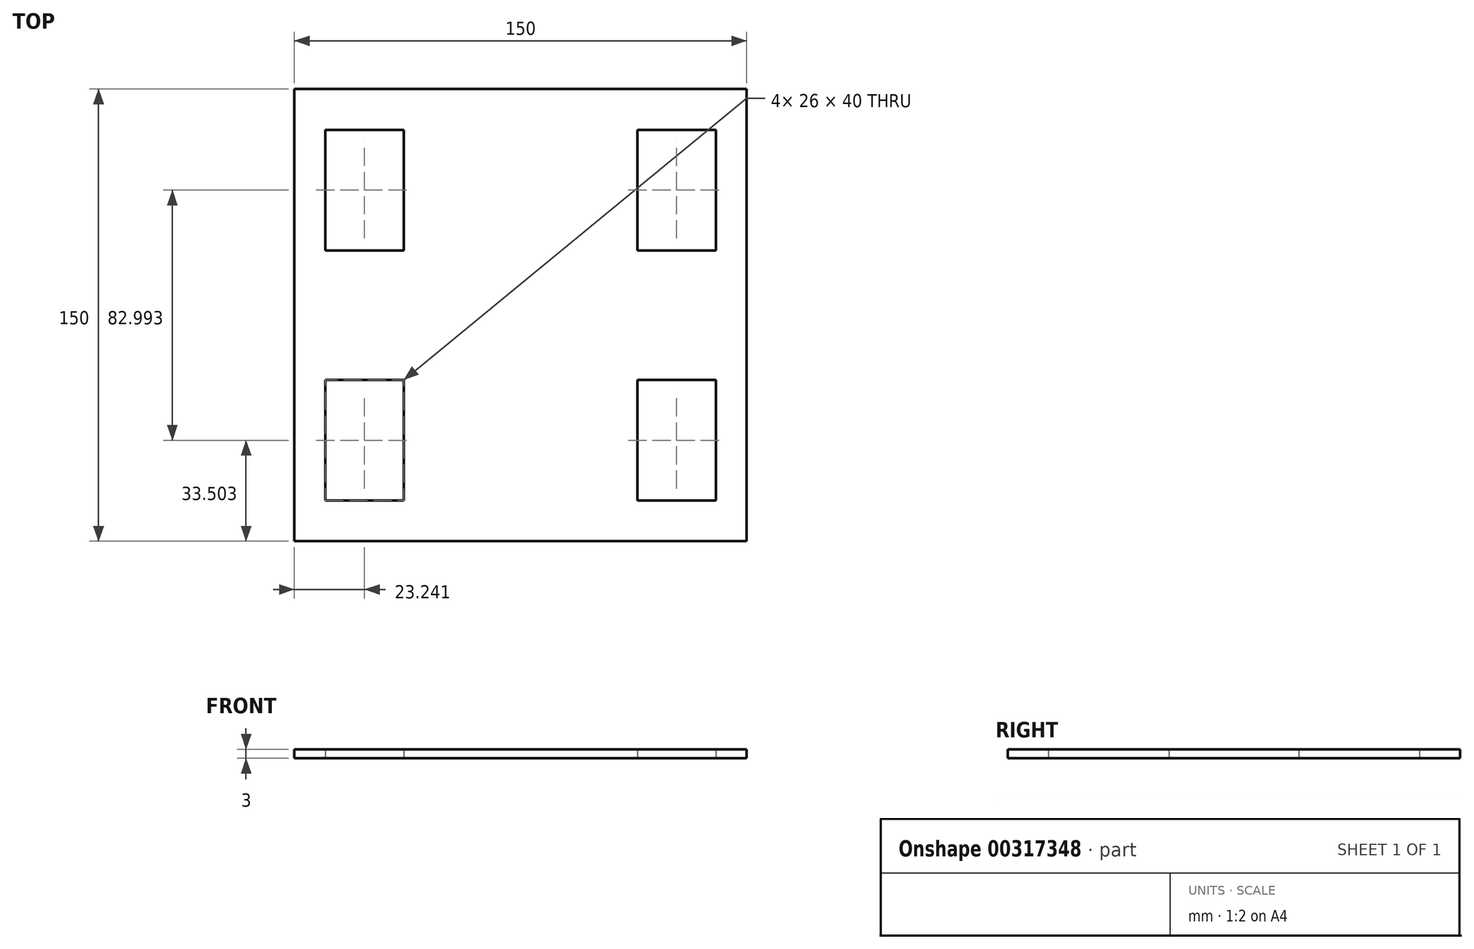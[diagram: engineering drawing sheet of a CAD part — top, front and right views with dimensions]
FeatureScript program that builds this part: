
annotation { "Feature Type Name" : "Feature", "Feature Type Description" : "" }
export const myFeature = defineFeature(function(context is Context, id is Id, definition is map)
    precondition{}
    {
        {
            var Q0;
            Q0=qCreatedBy(makeId("Top.planeOp"),FACE);
            var sketch = newSketch(context, id + "F0", { "sketchPlane" : qUnion([Q0])});
            skLineSegment(sketch, "E0.bottom", {"start": v(75, 75) * mm, "end": v(-75, 75) * mm});
            skLineSegment(sketch, "E0.top", {"start": v(75, -75) * mm, "end": v(-75, -75) * mm});
            skLineSegment(sketch, "E0.left", {"start": v(75, 75) * mm, "end": v(75, -75) * mm});
            skLineSegment(sketch, "E0.right", {"start": v(-75, 75) * mm, "end": v(-75, -75) * mm});
            skPoint(sketch, "E0.middle", {"position": v(0, 0) * mm});
            skLineSegment(sketch, "E1.bottom", {"start": v(-64.76, 61.5) * mm, "end": v(-38.76, 61.5) * mm});
            skLineSegment(sketch, "E1.top", {"start": v(-64.76, 21.5) * mm, "end": v(-38.76, 21.5) * mm});
            skLineSegment(sketch, "E1.left", {"start": v(-64.76, 61.5) * mm, "end": v(-64.76, 21.5) * mm});
            skLineSegment(sketch, "E1.right", {"start": v(-38.76, 61.5) * mm, "end": v(-38.76, 21.5) * mm});
            skLineSegment(sketch, "E2.MirrorCS", {"start": v(38.76, 61.5) * mm, "end": v(38.76, 21.5) * mm});
            skLineSegment(sketch, "E3.MirrorCS", {"start": v(64.76, 61.5) * mm, "end": v(64.76, 21.5) * mm});
            skLineSegment(sketch, "E4.MirrorCS", {"start": v(64.76, 61.5) * mm, "end": v(38.76, 61.5) * mm});
            skLineSegment(sketch, "E5.MirrorCS", {"start": v(64.76, 21.5) * mm, "end": v(38.76, 21.5) * mm});
            skLineSegment(sketch, "E6.MirrorCS", {"start": v(64.76, -21.5) * mm, "end": v(38.76, -21.5) * mm});
            skLineSegment(sketch, "E7.MirrorCS", {"start": v(64.76, -61.5) * mm, "end": v(38.76, -61.5) * mm});
            skLineSegment(sketch, "E8.MirrorCS", {"start": v(64.76, -61.5) * mm, "end": v(64.76, -21.5) * mm});
            skLineSegment(sketch, "E9.MirrorCS", {"start": v(38.76, -61.5) * mm, "end": v(38.76, -21.5) * mm});
            skLineSegment(sketch, "E10.MirrorCS", {"start": v(-38.76, -61.5) * mm, "end": v(-38.76, -21.5) * mm});
            skLineSegment(sketch, "E11.MirrorCS", {"start": v(-64.76, -61.5) * mm, "end": v(-64.76, -21.5) * mm});
            skLineSegment(sketch, "E12.MirrorCS", {"start": v(-64.76, -61.5) * mm, "end": v(-38.76, -61.5) * mm});
            skLineSegment(sketch, "E13.MirrorCS", {"start": v(-64.76, -21.5) * mm, "end": v(-38.76, -21.5) * mm});
            skLineSegment(sketch, "E14.bottom", {"start": v(-75, -75) * mm, "end": v(75, -75) * mm});
            skLineSegment(sketch, "E14.top", {"start": v(-75, -100) * mm, "end": v(75, -100) * mm});
            skLineSegment(sketch, "E14.left", {"start": v(-75, -75) * mm, "end": v(-75, -100) * mm});
            skLineSegment(sketch, "E14.right", {"start": v(75, -75) * mm, "end": v(75, -100) * mm});
            skLineSegment(sketch, "E15.0", {"start": v(-72, 72) * mm, "end": v(-72, -72) * mm});
            skLineSegment(sketch, "E15.1", {"start": v(72, 72) * mm, "end": v(-72, 72) * mm});
            skLineSegment(sketch, "E15.2", {"start": v(72, 72) * mm, "end": v(72, -72) * mm});
            skLineSegment(sketch, "E15.3", {"start": v(72, -72) * mm, "end": v(-72, -72) * mm});
            skSolve(sketch);
        }
        {
            var Q0;
            Q0=makeQuery(id+"F0.imprint","IMPRINT",FACE,{"disambiguationData":[TD([[makeQuery(id+"F0.imprint","IMPRINT",EDGE,{"derivedFrom":sQuery(id+"F0.wireOp",EDGE,"E1.bottom")}),1.0]])]});
            var Q1;
            Q1=makeQuery(id+"F0.imprint","IMPRINT",FACE,{"disambiguationData":[TD([[makeQuery(id+"F0.imprint","IMPRINT",EDGE,{"derivedFrom":sQuery(id+"F0.wireOp",EDGE,"E0.bottom")}),1.0]])]});
            extrude(context, id + "F1", {"entities" : qUnion([Q0, Q1]), "depth" : 3 * mm});
        }
    });
